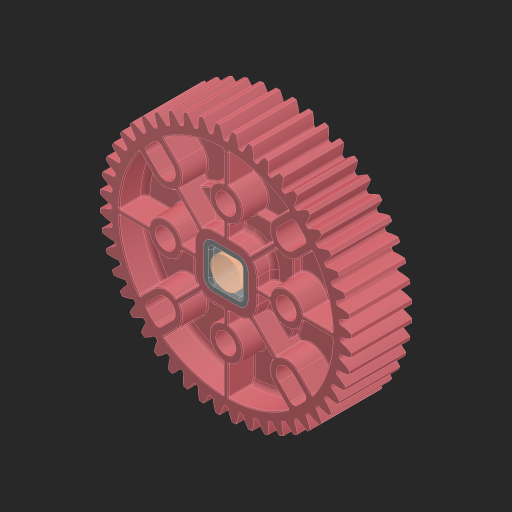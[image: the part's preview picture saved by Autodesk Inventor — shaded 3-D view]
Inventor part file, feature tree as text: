
AUTODESK INVENTOR PART (.ipt)
format: ipt  version: 2023 (Build 270158000, 158)  size: 2,622,976 bytes
history: native  units: in
note: dims shown in document units (in); Inventor stores cm internally (conversion verified against a paired STEP export)
features: other x3, sketch x1, extrude x1
ambient origin geometry x8: Origin, YZ Plane, XZ Plane, XY Plane, X Axis, Y Axis, Z Axis, Center Point
bodies: Solid1 (feature_tree), Solid2 (feature_tree)
feature tree (5):
  sketch  "Sketch1"  dims[d0=0.25in d1=0.3937in d2=0.0in]
  other  "Srf1"
  other  "276-7573-001_OVERMOLD Rev7_48T 24DP Gear_1:1"
  other  "276-7573-002 Rev7_2:1"
  extrude  "ExtrusionSrf1"  Depth=0.3937in TaperAngle=0.0deg
